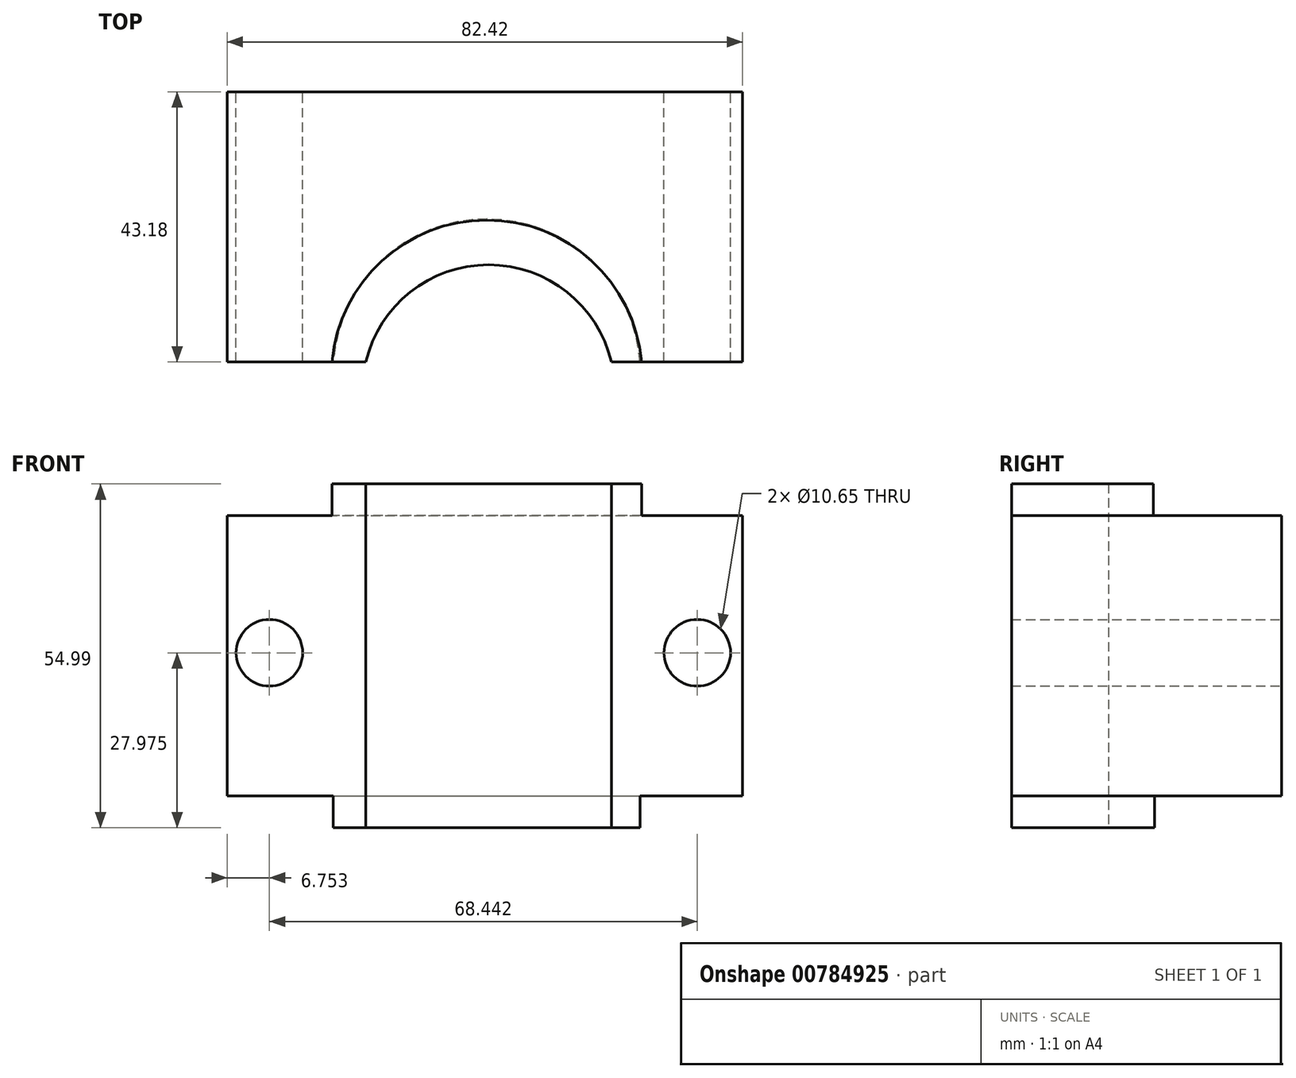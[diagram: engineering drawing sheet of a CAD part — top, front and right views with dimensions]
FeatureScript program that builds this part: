
annotation { "Feature Type Name" : "Feature", "Feature Type Description" : "" }
export const myFeature = defineFeature(function(context is Context, id is Id, definition is map)
    precondition{}
    {
        {
            var Q0;
            Q0=qCreatedBy(makeId("Front.planeOp"),FACE);
            var sketch = newSketch(context, id + "F0", { "sketchPlane" : qUnion([Q0])});
            skLineSegment(sketch, "E0.bottom", {"start": v(-44.95, 18.2) * mm, "end": v(37.47, 18.2) * mm});
            skLineSegment(sketch, "E0.top", {"start": v(-44.95, -26.63) * mm, "end": v(37.47, -26.63) * mm});
            skLineSegment(sketch, "E0.left", {"start": v(-44.95, 18.2) * mm, "end": v(-44.95, -26.63) * mm});
            skLineSegment(sketch, "E0.right", {"start": v(37.47, 18.2) * mm, "end": v(37.47, -26.63) * mm});
            skCircle(sketch, "E1", {"center": v(30.24, -3.74) * mm, "radius": 5.32 * mm});
            skCircle(sketch, "E2", {"center": v(-38.2, -3.74) * mm, "radius": 5.32 * mm});
            skSolve(sketch);
        }
        {
            var Q0;
            Q0 = qSketchRegion(id + "F0", true);
            extrude(context, id + "F1", {"entities" : qUnion([Q0]), "depth" : 43.18 * mm, "offsetDistance" : 25.4 * mm});
        }
        {
            var Q0;
            Q0=makeQuery(id+"F1.opExtrude","SWEPT_FACE",FACE,{"disambiguationData":[OSD([sQuery(id+"F0.wireOp",EDGE,"E0.top")])]});
            var sketch = newSketch(context, id + "F2", { "sketchPlane" : qUnion([Q0])});
            skArc(sketch, "E3", {"start": v(-22.77, 43.18) * mm, "mid": v(-3.13, 27.64) * mm, "end": v(16.5, 43.18) * mm});
            skLineSegment(sketch, "E4", {"start": v(-22.77, 43.18) * mm, "end": v(16.5, 43.18) * mm});
            skSolve(sketch);
        }
        {
            var Q0;
            Q0=makeQuery(id+"F2.imprint","IMPRINT",FACE,{"disambiguationData":[TD([[makeQuery(id+"F2.imprint","IMPRINT",EDGE,{"derivedFrom":sQuery(id+"F2.wireOp",EDGE,"E3")}),1.0]])]});
            extrude(context, id + "F3", {"entities" : qUnion([Q0]), "operationType" : NewBodyOperationType.REMOVE, "oppositeDirection" : true, "depth" : 50.8 * mm, "offsetDistance" : 25.4 * mm});
        }
        {
            var Q0;
            Q0=makeQuery(id+"F1.opExtrude","SWEPT_FACE",FACE,{"disambiguationData":[OSD([sQuery(id+"F0.wireOp",EDGE,"E0.top")])]});
            var sketch = newSketch(context, id + "F4", { "sketchPlane" : qUnion([Q0])});
            skArc(sketch, "E5", {"start": v(-27.97, 43.18) * mm, "mid": v(-3.45, 20.3) * mm, "end": v(21.07, 43.18) * mm});
            skSolve(sketch);
        }
        {
            var Q0;
            {var subQ0=sQuery(id+"F4.wireOp",EDGE,"E5");Q0=makeQuery(id+"F4.imprint","IMPRINT",FACE,{"disambiguationData":[TD([[makeQuery(id+"F4.imprint","IMPRINT",EDGE,{"derivedFrom":subQ0}),1.0]])]});}
            extrude(context, id + "F5", {"entities" : qUnion([Q0]), "operationType" : NewBodyOperationType.ADD, "depth" : 5.08 * mm, "offsetDistance" : 25.4 * mm});
        }
        {
            var Q0;
            Q0=makeQuery(id+"F1.opExtrude","SWEPT_FACE",FACE,{"disambiguationData":[OSD([sQuery(id+"F0.wireOp",EDGE,"E0.bottom")])]});
            var sketch = newSketch(context, id + "F6", { "sketchPlane" : qUnion([Q0])});
            skArc(sketch, "E6", {"start": v(21.33, -43.18) * mm, "mid": v(-3.43, -20.5) * mm, "end": v(-28.2, -43.18) * mm});
            skSolve(sketch);
        }
        {
            var Q0;
            {var subQ0=sQuery(id+"F6.wireOp",EDGE,"E6");Q0=makeQuery(id+"F6.imprint","IMPRINT",FACE,{"disambiguationData":[TD([[makeQuery(id+"F6.imprint","IMPRINT",EDGE,{"derivedFrom":subQ0}),1.0]])]});}
            extrude(context, id + "F7", {"entities" : qUnion([Q0]), "operationType" : NewBodyOperationType.ADD, "depth" : 5.08 * mm, "offsetDistance" : 25.4 * mm});
        }
    });
